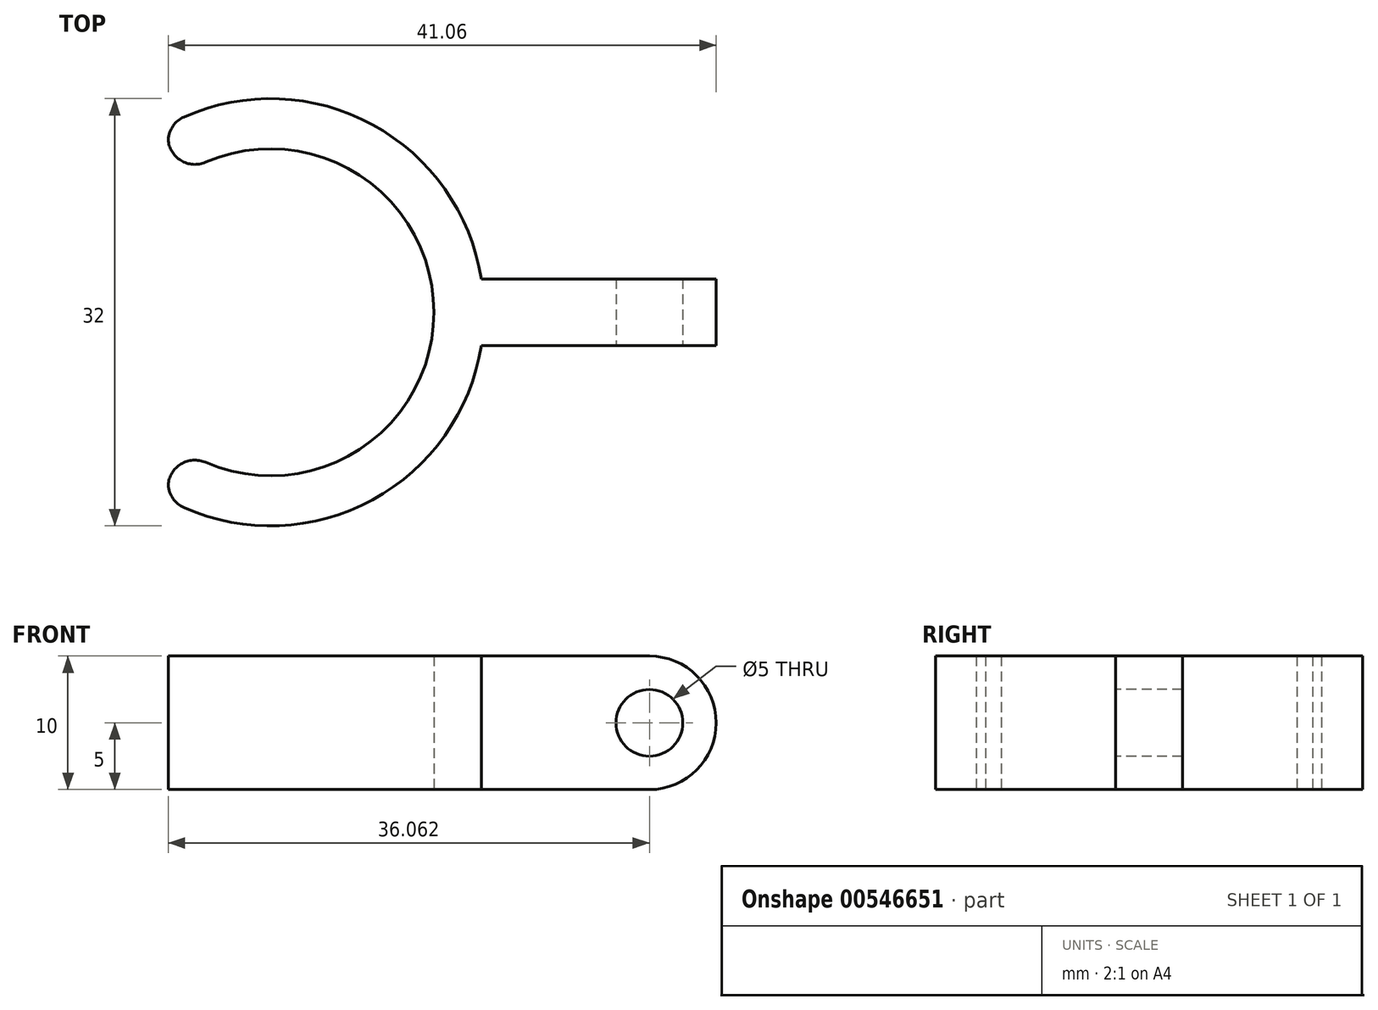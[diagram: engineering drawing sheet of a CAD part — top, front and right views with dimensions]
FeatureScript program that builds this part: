
annotation { "Feature Type Name" : "Feature", "Feature Type Description" : "" }
export const myFeature = defineFeature(function(context is Context, id is Id, definition is map)
    precondition{}
    {
        {
            var Q0;
            Q0=qCreatedBy(makeId("Top.planeOp"),FACE);
            var sketch = newSketch(context, id + "F0", { "sketchPlane" : qUnion([Q0])});
            skCircle(sketch, "E0", {"center": v(0, 0) * mm, "radius": 16 * mm});
            skCircle(sketch, "E1", {"center": v(0, 0) * mm, "radius": 12.25 * mm});
            skSolve(sketch);
        }
        {
            var Q0;
            Q0=qSketchRegion(id+"F0",true);
            extrude(context, id + "F1", {"entities" : qUnion([Q0]), "depth" : 10 * mm, "offsetDistance" : 25 * mm});
        }
        {
            var Q0;
            Q0=makeQuery(id+"F1.opExtrude","CAP_FACE",FACE,{"disambiguationData":[OSD([sQuery(id+"F0.wireOp",EDGE,"E0"),sQuery(id+"F0.wireOp",EDGE,"E1")])],"isStart":false});
            var sketch = newSketch(context, id + "F2", { "sketchPlane" : qUnion([Q0])});
            skLineSegment(sketch, "E2.bottom", {"start": v(-19.12, 16.48) * mm, "end": v(-7.67, 16.48) * mm});
            skLineSegment(sketch, "E2.top", {"start": v(-19.12, -16) * mm, "end": v(-7.67, -16) * mm});
            skLineSegment(sketch, "E2.left", {"start": v(-19.12, 16.48) * mm, "end": v(-19.12, -16) * mm});
            skLineSegment(sketch, "E2.right", {"start": v(-7.67, 16.48) * mm, "end": v(-7.67, -16) * mm});
            skSolve(sketch);
        }
        {
            var Q0;
            Q0=qSketchRegion(id+"F2",true);
            extrude(context, id + "F3", {"entities" : qUnion([Q0]), "operationType" : NewBodyOperationType.REMOVE, "endBound" : BoundingType.THROUGH_ALL, "oppositeDirection" : true, "depth" : 25 * mm, "offsetDistance" : 25 * mm});
        }
        {
            var Q0;
            Q0=makeQuery(id+"F3.boolean.opBoolean","INTERSECT",EDGE,{"disambiguationData":[OD(1.0)],"derivedFrom":[makeQuery(id+"F1.opExtrude","SWEPT_FACE",FACE,{"disambiguationData":[OSD([sQuery(id+"F0.wireOp",EDGE,"E1")])]}),makeQuery(id+"F3.opExtrude","SWEPT_FACE",FACE,{"disambiguationData":[OSD([sQuery(id+"F2.wireOp",EDGE,"E2.right")])]})]});
            var Q1;
            Q1=makeQuery(id+"F3.boolean.opBoolean","INTERSECT",EDGE,{"disambiguationData":[OD(0.0)],"derivedFrom":[makeQuery(id+"F1.opExtrude","SWEPT_FACE",FACE,{"disambiguationData":[OSD([sQuery(id+"F0.wireOp",EDGE,"E1")])]}),makeQuery(id+"F3.opExtrude","SWEPT_FACE",FACE,{"disambiguationData":[OSD([sQuery(id+"F2.wireOp",EDGE,"E2.right")])]})]});
            var Q2;
            Q2=makeQuery(id+"F3.boolean.opBoolean","INTERSECT",EDGE,{"disambiguationData":[OD(1.0)],"derivedFrom":[makeQuery(id+"F1.opExtrude","SWEPT_FACE",FACE,{"disambiguationData":[OSD([sQuery(id+"F0.wireOp",EDGE,"E0")])]}),makeQuery(id+"F3.opExtrude","SWEPT_FACE",FACE,{"disambiguationData":[OSD([sQuery(id+"F2.wireOp",EDGE,"E2.right")])]})]});
            var Q3;
            Q3=makeQuery(id+"F3.boolean.opBoolean","INTERSECT",EDGE,{"disambiguationData":[OD(0.0)],"derivedFrom":[makeQuery(id+"F1.opExtrude","SWEPT_FACE",FACE,{"disambiguationData":[OSD([sQuery(id+"F0.wireOp",EDGE,"E0")])]}),makeQuery(id+"F3.opExtrude","SWEPT_FACE",FACE,{"disambiguationData":[OSD([sQuery(id+"F2.wireOp",EDGE,"E2.right")])]})]});
            fillet(context, id + "F4", {"entities" : qUnion([Q0, Q1, Q2, Q3]), "radius" : 2 * mm, "tangentPropagation" : true, "allowEdgeOverflow" : false});
        }
        {
            var Q0;
            Q0=makeQuery(id+"F1.opExtrude","CAP_FACE",FACE,{"disambiguationData":[OSD([sQuery(id+"F0.wireOp",EDGE,"E0"),sQuery(id+"F0.wireOp",EDGE,"E1")])],"isStart":false});
            var sketch = newSketch(context, id + "F5", { "sketchPlane" : qUnion([Q0])});
            skLineSegment(sketch, "E3.bottom", {"start": v(33.4, -2.5) * mm, "end": v(13.4, -2.5) * mm});
            skLineSegment(sketch, "E3.top", {"start": v(33.4, 2.5) * mm, "end": v(13.4, 2.5) * mm});
            skLineSegment(sketch, "E3.left", {"start": v(33.4, -2.5) * mm, "end": v(33.4, 2.5) * mm});
            skLineSegment(sketch, "E3.right", {"start": v(13.4, -2.5) * mm, "end": v(13.4, 2.5) * mm});
            skPoint(sketch, "E3.middle", {"position": v(23.4, 0) * mm});
            skSolve(sketch);
        }
        {
            var Q0;
            Q0=qSketchRegion(id+"F5",true);
            extrude(context, id + "F6", {"entities" : qUnion([Q0]), "operationType" : NewBodyOperationType.ADD, "oppositeDirection" : true, "depth" : 10 * mm, "offsetDistance" : 25 * mm});
        }
        {
            var Q0;
            Q0=makeQuery(id+"F6.opExtrude","SWEPT_FACE",FACE,{"disambiguationData":[OSD([sQuery(id+"F5.wireOp",EDGE,"E3.bottom")])]});
            var sketch = newSketch(context, id + "F7", { "sketchPlane" : qUnion([Q0])});
            skCircle(sketch, "E4", {"center": v(28.4, 5) * mm, "radius": 2.5 * mm});
            skSolve(sketch);
        }
        {
            var Q0;
            Q0=makeQuery(id+"F7.imprint","IMPRINT",FACE,{"disambiguationData":[TD([[makeQuery(id+"F7.imprint","IMPRINT",EDGE,{"derivedFrom":sQuery(id+"F7.wireOp",EDGE,"E4")}),1.0]])]});
            extrude(context, id + "F8", {"entities" : qUnion([Q0]), "operationType" : NewBodyOperationType.REMOVE, "endBound" : BoundingType.THROUGH_ALL, "oppositeDirection" : true, "depth" : 25 * mm, "offsetDistance" : 25 * mm});
        }
        {
            var Q0;
            Q0=makeQuery(id+"F6.opExtrude","CAP_EDGE",EDGE,{"disambiguationData":[OSD([sQuery(id+"F5.wireOp",EDGE,"E3.left")])],"isStart":true});
            var Q1;
            Q1=makeQuery(id+"F6.opExtrude","CAP_EDGE",EDGE,{"disambiguationData":[OSD([sQuery(id+"F5.wireOp",EDGE,"E3.left")])],"isStart":false});
            fillet(context, id + "F9", {"entities" : qUnion([Q0, Q1]), "radius" : 5 * mm, "tangentPropagation" : true, "allowEdgeOverflow" : false});
        }
    });
